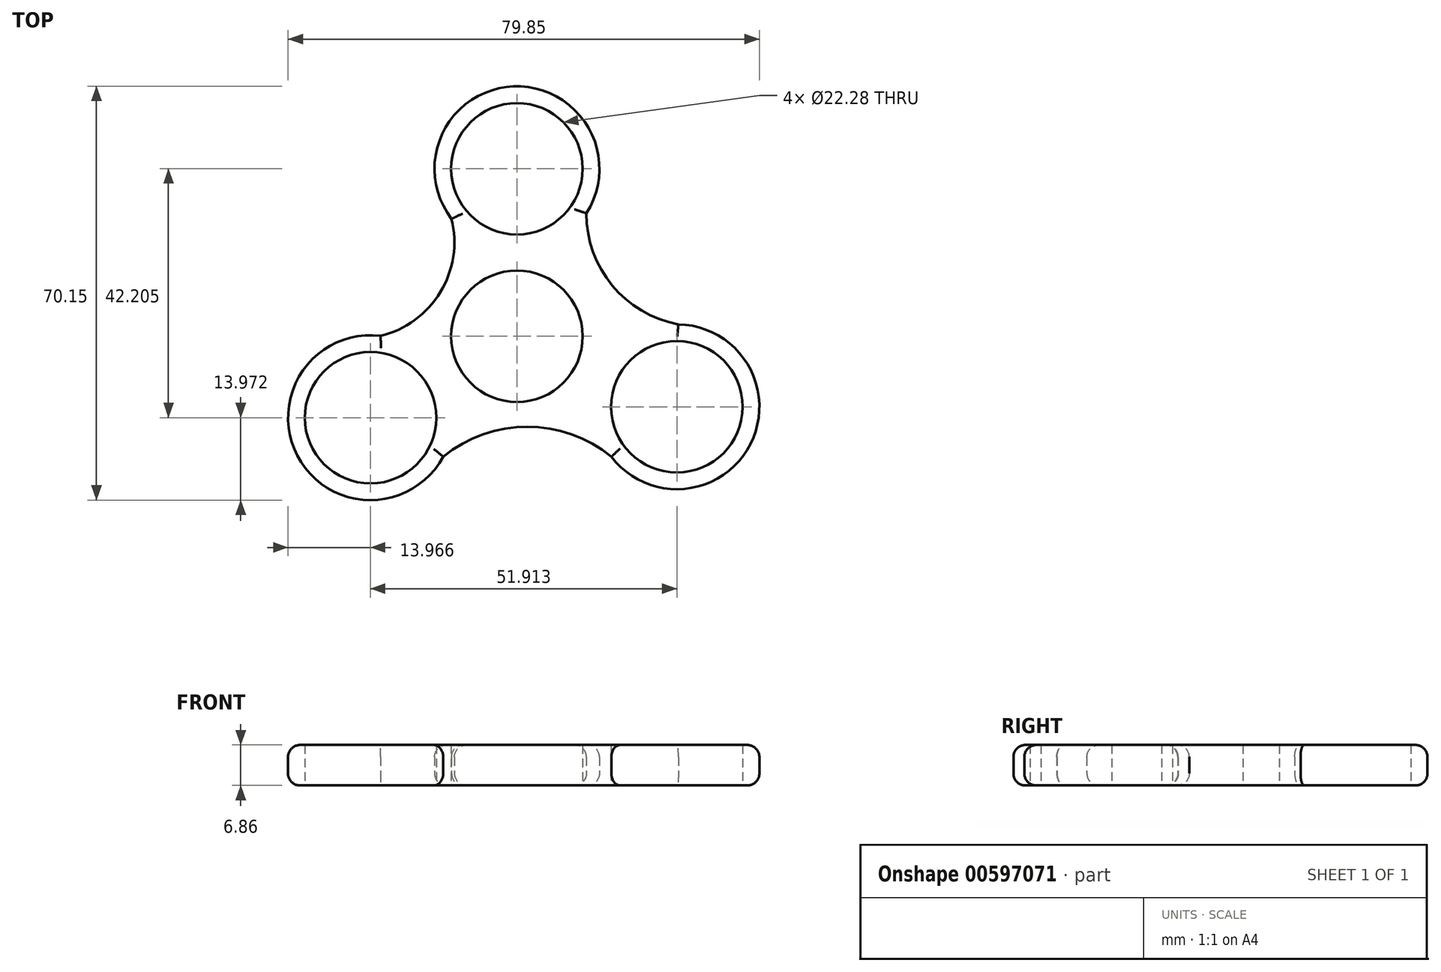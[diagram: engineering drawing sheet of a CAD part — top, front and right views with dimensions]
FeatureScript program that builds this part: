
annotation { "Feature Type Name" : "Feature", "Feature Type Description" : "" }
export const myFeature = defineFeature(function(context is Context, id is Id, definition is map)
    precondition{}
    {
        {
            var Q0;
            Q0=qCreatedBy(makeId("Top.planeOp"),FACE);
            var sketch = newSketch(context, id + "F0", { "sketchPlane" : qUnion([Q0])});
            skCircle(sketch, "E0", {"center": v(0, 0) * mm, "radius": 11.14 * mm});
            skCircle(sketch, "E1", {"center": v(0, 28.4) * mm, "radius": 11.14 * mm});
            skCircle(sketch, "E2", {"center": v(-24.81, -13.8) * mm, "radius": 11.14 * mm});
            skCircle(sketch, "E3", {"center": v(27.1, -11.95) * mm, "radius": 11.14 * mm});
            skArc(sketch, "E4", {"start": v(-23.12, 0.06) * mm, "mid": v(-37.21, -20.25) * mm, "end": v(-12.5, -20.4) * mm});
            skArc(sketch, "E5", {"start": v(16, -20.44) * mm, "mid": v(39.57, -18.26) * mm, "end": v(27.35, 2.02) * mm});
            skArc(sketch, "E6", {"start": v(11.77, 20.87) * mm, "mid": v(-0.6, 42.35) * mm, "end": v(-11.08, 19.89) * mm});
            skArc(sketch, "E7", {"start": v(-23.12, 0.06) * mm, "mid": v(-12.98, 7.47) * mm, "end": v(-11.08, 19.89) * mm});
            skArc(sketch, "E8", {"start": v(11.77, 20.87) * mm, "mid": v(16.14, 8.61) * mm, "end": v(27.35, 2.02) * mm});
            skArc(sketch, "E9", {"start": v(16, -20.44) * mm, "mid": v(1.76, -15.34) * mm, "end": v(-12.5, -20.4) * mm});
            skSolve(sketch);
        }
        {
            var Q0;
            Q0 = qSketchRegion(id + "F0", true);
            extrude(context, id + "F1", {"entities" : qUnion([Q0]), "depth" : 6.86 * mm, "offsetDistance" : 25.4 * mm});
        }
        {
            var Q0;
            Q0=makeQuery(id+"F1.opExtrude","CAP_EDGE",EDGE,{"disambiguationData":[OSD([sQuery(id+"F0.wireOp",EDGE,"E9")])],"isStart":false});
            var Q1;
            Q1=makeQuery(id+"F1.opExtrude","CAP_EDGE",EDGE,{"disambiguationData":[OSD([sQuery(id+"F0.wireOp",EDGE,"E4")])],"isStart":false});
            var Q2;
            Q2=makeQuery(id+"F1.opExtrude","CAP_EDGE",EDGE,{"disambiguationData":[OSD([sQuery(id+"F0.wireOp",EDGE,"E7")])],"isStart":false});
            var Q3;
            Q3=makeQuery(id+"F1.opExtrude","CAP_EDGE",EDGE,{"disambiguationData":[OSD([sQuery(id+"F0.wireOp",EDGE,"E6")])],"isStart":false});
            var Q4;
            Q4=makeQuery(id+"F1.opExtrude","CAP_EDGE",EDGE,{"disambiguationData":[OSD([sQuery(id+"F0.wireOp",EDGE,"E5")])],"isStart":false});
            var Q5;
            Q5=makeQuery(id+"F1.opExtrude","CAP_EDGE",EDGE,{"disambiguationData":[OSD([sQuery(id+"F0.wireOp",EDGE,"E8")])],"isStart":false});
            var Q6;
            Q6=makeQuery(id+"F1.opExtrude","CAP_EDGE",EDGE,{"disambiguationData":[OSD([sQuery(id+"F0.wireOp",EDGE,"E9")])],"isStart":true});
            var Q7;
            Q7=makeQuery(id+"F1.opExtrude","CAP_EDGE",EDGE,{"disambiguationData":[OSD([sQuery(id+"F0.wireOp",EDGE,"E4")])],"isStart":true});
            var Q8;
            Q8=makeQuery(id+"F1.opExtrude","CAP_EDGE",EDGE,{"disambiguationData":[OSD([sQuery(id+"F0.wireOp",EDGE,"E5")])],"isStart":true});
            var Q9;
            Q9=makeQuery(id+"F1.opExtrude","CAP_EDGE",EDGE,{"disambiguationData":[OSD([sQuery(id+"F0.wireOp",EDGE,"E7")])],"isStart":true});
            var Q10;
            Q10=makeQuery(id+"F1.opExtrude","CAP_EDGE",EDGE,{"disambiguationData":[OSD([sQuery(id+"F0.wireOp",EDGE,"E6")])],"isStart":true});
            var Q11;
            Q11=makeQuery(id+"F1.opExtrude","CAP_EDGE",EDGE,{"disambiguationData":[OSD([sQuery(id+"F0.wireOp",EDGE,"E8")])],"isStart":true});
            fillet(context, id + "F2", {"entities" : qUnion([Q0, Q1, Q2, Q3, Q4, Q5, Q6, Q7, Q8, Q9, Q10, Q11]), "radius" : 2.03 * mm, "tangentPropagation" : true, "allowEdgeOverflow" : false});
        }
    });
